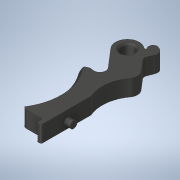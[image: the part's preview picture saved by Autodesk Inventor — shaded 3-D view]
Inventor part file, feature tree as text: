
AUTODESK INVENTOR PART (.ipt)
format: ipt  version: 2020.1 (Build 241239000, 239)  size: 346,624 bytes
history: native  units: mm
features: sketch x4, extrude x3, fillet x2, other x2, plane x1, revolve x1, mirror x1, chamfer x1
ambient origin geometry x8: Origin, YZ Plane, XZ Plane, XY Plane, X Axis, Y Axis, Z Axis, Center Point
bodies: Solid1 (feature_tree)
feature tree (15):
  extrude  "Extrusion1"  Depth=15.0mm
  plane  "Work Plane1"
  revolve  "Revolution1"  [1 undecoded]
  mirror  "Mirror1"
  chamfer  "Chamfer1"  Distance=3.0mm
  extrude  "Extrusion3"  Depth=12.0mm
  fillet  "Fillet1"  Radius=3.0mm
  fillet  "Fillet2"  Radius=1.5mm
  extrude  "Extrusion2"  Depth=0.2mm
  sketch  "Sketch1"  dims[d5=7.0mm d6=15.0mm]
  other  "Image1"
  other  "Work Axis1"
  sketch  "Sketch2"  dims[d7=8.0mm d8=4.4mm]
  sketch  "Sketch3"  dims[d9=2.0mm]
  sketch  "Sketch4"  dims[d10=35.0mm d14=3.0mm d18=12.0mm d93=3.0mm d94=1.5mm d96=3.839724mm d97=5.6mm d98=0.0mm d99=90.0deg d101=1.0mm d103=0.5mm d104=90.0deg d105=90.0deg d106=0.5mm d107=2.0mm d108=45.0deg d109=0.5mm d110=1.25mm d115=0.7mm d116=150.0deg d121=0.5mm d123=1.5mm d124=2.0mm d125=0.5mm d140=1.5mm d141=2.0mm d149=2.4mm d151=8.0mm d152=2.0mm d153=0.0mm d154=2.15mm d155=0.2mm d156=0.0mm]
note: 1 required parameter value undecoded (feature->parameter linkage not recoverable at this tier; creation-order binding heuristic only, values carry confidence <= 0.55)
